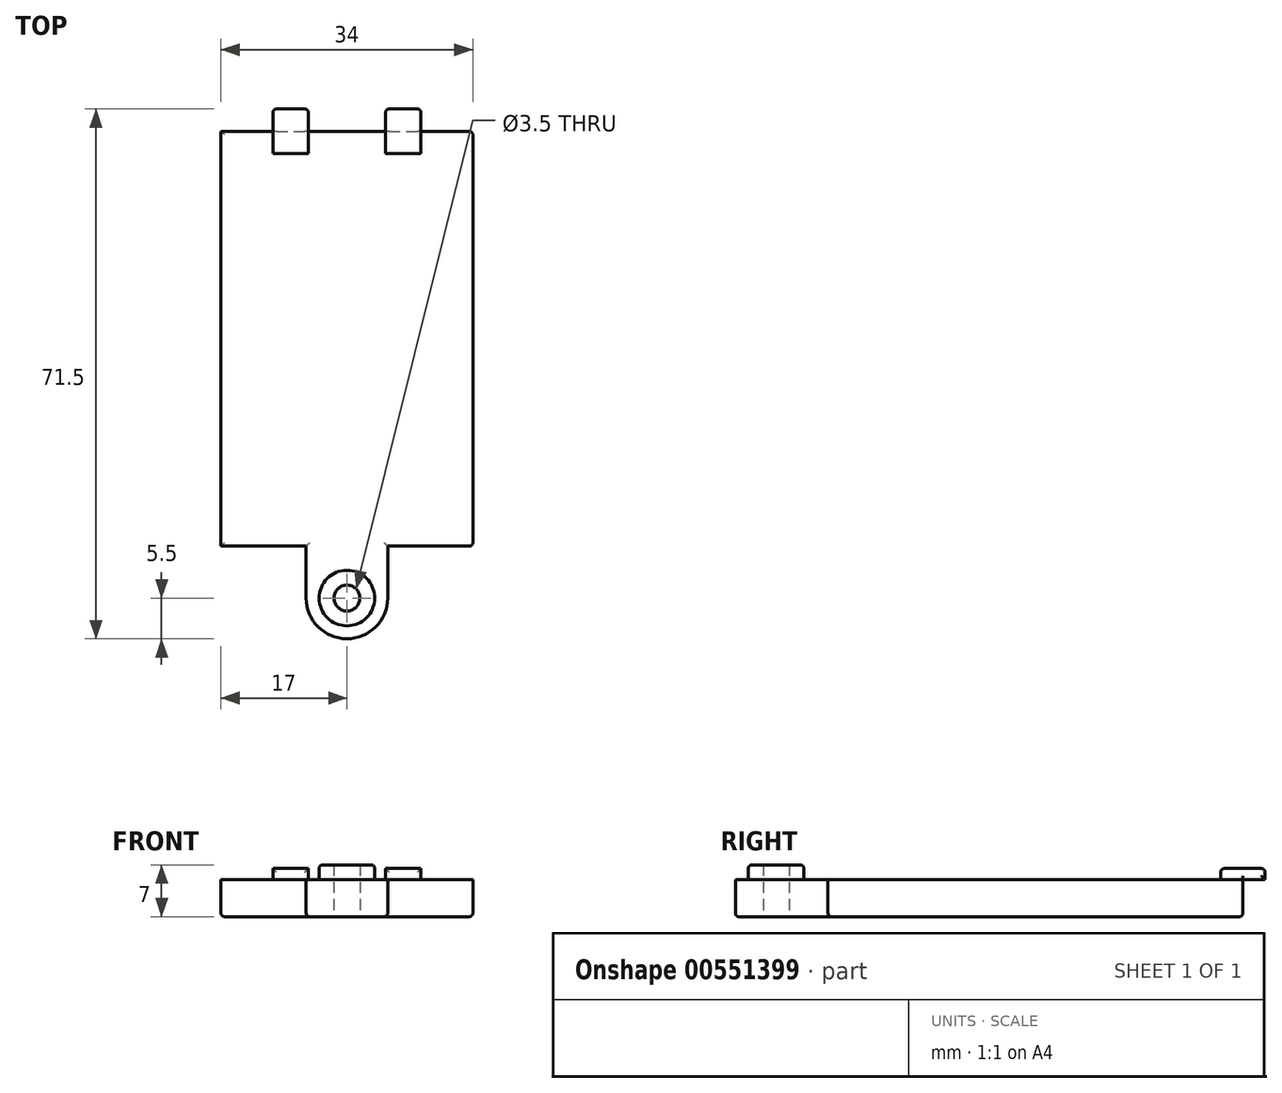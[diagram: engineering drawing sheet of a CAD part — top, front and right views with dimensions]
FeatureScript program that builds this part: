
annotation { "Feature Type Name" : "Feature", "Feature Type Description" : "" }
export const myFeature = defineFeature(function(context is Context, id is Id, definition is map)
    precondition{}
    {
        {
            var Q0;
            Q0=qCreatedBy(makeId("Top.planeOp"),FACE);
            var sketch = newSketch(context, id + "F0", { "sketchPlane" : qUnion([Q0])});
            skLineSegment(sketch, "E0.bottom", {"start": v(-17, 29) * mm, "end": v(17, 29) * mm});
            skLineSegment(sketch, "E0.top", {"start": v(-17, -27) * mm, "end": v(17, -27) * mm});
            skLineSegment(sketch, "E0.left", {"start": v(-17, 29) * mm, "end": v(-17, -27) * mm});
            skLineSegment(sketch, "E0.right", {"start": v(17, 29) * mm, "end": v(17, -27) * mm});
            skCircle(sketch, "E1", {"center": v(0, -34) * mm, "radius": 5.5 * mm});
            skLineSegment(sketch, "E2", {"start": v(5.5, -34) * mm, "end": v(5.5, -27) * mm});
            skLineSegment(sketch, "E3", {"start": v(-5.5, -34) * mm, "end": v(-5.5, -27) * mm});
            skSolve(sketch);
        }
        {
            var Q0;
            Q0 = qSketchRegion(id + "F0", true);
            extrude(context, id + "F1", {"entities" : qUnion([Q0]), "depth" : 5 * mm, "offsetDistance" : 25 * mm});
        }
        {
            var Q0;
            Q0=makeQuery(id+"F1.opExtrude","CAP_FACE",FACE,{"disambiguationData":[OSD([sQuery(id+"F0.wireOp",EDGE,"E0.bottom"),sQuery(id+"F0.wireOp",EDGE,"E0.top"),sQuery(id+"F0.wireOp",EDGE,"E0.left"),sQuery(id+"F0.wireOp",EDGE,"E0.right"),sQuery(id+"F0.wireOp",EDGE,"E1"),sQuery(id+"F0.wireOp",EDGE,"E2"),sQuery(id+"F0.wireOp",EDGE,"E3")])],"isStart":false});
            var sketch = newSketch(context, id + "F2", { "sketchPlane" : qUnion([Q0])});
            skCircle(sketch, "E4", {"center": v(0, -34) * mm, "radius": 3.75 * mm});
            skSolve(sketch);
        }
        {
            var Q0;
            Q0 = qSketchRegion(id + "F2", true);
            extrude(context, id + "F3", {"entities" : qUnion([Q0]), "operationType" : NewBodyOperationType.ADD, "depth" : 2 * mm, "offsetDistance" : 25 * mm});
        }
        {
            var Q0;
            Q0=sQuery(id+"F0.wireOp",VERTEX,"E1.center");
            var Q1;
            Q1=makeQuery(id+"F1.opExtrude","SWEPT_BODY",BODY,{"disambiguationData":[OSD([sQuery(id+"F0.wireOp",EDGE,"E0.bottom"),sQuery(id+"F0.wireOp",EDGE,"E0.top"),sQuery(id+"F0.wireOp",EDGE,"E0.left"),sQuery(id+"F0.wireOp",EDGE,"E0.right"),sQuery(id+"F0.wireOp",EDGE,"E1"),sQuery(id+"F0.wireOp",EDGE,"E2"),sQuery(id+"F0.wireOp",EDGE,"E3")])]});
            hole(context, id + "F4", {"style" : HoleStyle.SIMPLE, "endStyle" : HoleEndStyle.THROUGH, "oppositeDirection" : true, "holeDiameter" : 3.5 * mm, "tappedDepth" : 12 * mm, "tapClearance" : 3, "locations" : qUnion([Q0]), "scope" : qUnion([Q1])});
        }
        {
            var Q0;
            Q0=makeQuery(id+"F1.opExtrude","CAP_FACE",FACE,{"disambiguationData":[OSD([sQuery(id+"F0.wireOp",EDGE,"E0.bottom"),sQuery(id+"F0.wireOp",EDGE,"E0.top"),sQuery(id+"F0.wireOp",EDGE,"E0.left"),sQuery(id+"F0.wireOp",EDGE,"E0.right"),sQuery(id+"F0.wireOp",EDGE,"E1"),sQuery(id+"F0.wireOp",EDGE,"E2"),sQuery(id+"F0.wireOp",EDGE,"E3")])],"isStart":false});
            var sketch = newSketch(context, id + "F5", { "sketchPlane" : qUnion([Q0])});
            skLineSegment(sketch, "E5.bottom", {"start": v(-10, 26) * mm, "end": v(-5.2, 26) * mm});
            skLineSegment(sketch, "E5.top", {"start": v(-10, 32) * mm, "end": v(-5.2, 32) * mm});
            skLineSegment(sketch, "E5.left", {"start": v(-10, 26) * mm, "end": v(-10, 32) * mm});
            skLineSegment(sketch, "E5.right", {"start": v(-5.2, 26) * mm, "end": v(-5.2, 32) * mm});
            skLineSegment(sketch, "E6.bottom", {"start": v(5.2, 26) * mm, "end": v(10, 26) * mm});
            skLineSegment(sketch, "E6.top", {"start": v(5.2, 32) * mm, "end": v(10, 32) * mm});
            skLineSegment(sketch, "E6.left", {"start": v(5.2, 26) * mm, "end": v(5.2, 32) * mm});
            skLineSegment(sketch, "E6.right", {"start": v(10, 26) * mm, "end": v(10, 32) * mm});
            skSolve(sketch);
        }
        {
            var Q0;
            Q0 = qSketchRegion(id + "F5", true);
            extrude(context, id + "F6", {"entities" : qUnion([Q0]), "operationType" : NewBodyOperationType.ADD, "depth" : 1.5 * mm, "offsetDistance" : 25 * mm});
        }
        {
            var Q0;
            Q0=makeQuery(id+"F6.opExtrude","CAP_EDGE",EDGE,{"disambiguationData":[OSD([sQuery(id+"F5.wireOp",EDGE,"E6.bottom")])],"isStart":false});
            var Q1;
            Q1=makeQuery(id+"F6.opExtrude","CAP_EDGE",EDGE,{"disambiguationData":[OSD([sQuery(id+"F5.wireOp",EDGE,"E5.bottom")])],"isStart":false});
            var Q2;
            Q2=makeQuery(id+"F6.opExtrude","CAP_EDGE",EDGE,{"disambiguationData":[OSD([sQuery(id+"F5.wireOp",EDGE,"E5.top")])],"isStart":false});
            var Q3;
            Q3=makeQuery(id+"F6.opExtrude","CAP_EDGE",EDGE,{"disambiguationData":[OSD([sQuery(id+"F5.wireOp",EDGE,"E6.top")])],"isStart":false});
            var Q4;
            Q4=makeQuery(id+"F1.opExtrude","CAP_EDGE",EDGE,{"disambiguationData":[OSD([sQuery(id+"F0.wireOp",EDGE,"E0.bottom")])],"isStart":true});
            var Q5;
            Q5=makeQuery(id+"F1.opExtrude","SWEPT_EDGE",EDGE,{"disambiguationData":[OSD([sQuery(id+"F0.wireOp",EDGE,"E0.bottom"),sQuery(id+"F0.wireOp",EDGE,"E0.right")])]});
            var Q6;
            Q6=makeQuery(id+"F1.opExtrude","CAP_EDGE",EDGE,{"disambiguationData":[OSD([sQuery(id+"F0.wireOp",EDGE,"E0.right")])],"isStart":true});
            var Q7;
            Q7=makeQuery(id+"F1.opExtrude","SWEPT_EDGE",EDGE,{"disambiguationData":[OSD([sQuery(id+"F0.wireOp",EDGE,"E0.top"),sQuery(id+"F0.wireOp",EDGE,"E0.right")])]});
            var Q8;
            Q8=makeQuery(id+"F1.opExtrude","CAP_EDGE",EDGE,{"disambiguationData":[OSD([sQuery(id+"F0.wireOp",EDGE,"E2")])],"isStart":true});
            var Q9;
            Q9=makeQuery(id+"F1.opExtrude","CAP_EDGE",EDGE,{"disambiguationData":[OSD([sQuery(id+"F0.wireOp",EDGE,"E1")])],"isStart":true});
            var Q10;
            Q10=makeQuery(id+"F3.opExtrude","CAP_EDGE",EDGE,{"disambiguationData":[OSD([sQuery(id+"F2.wireOp",EDGE,"E4")])],"isStart":false});
            var Q11;
            {var subQ0=sQuery(id+"F0.wireOp",EDGE,"E0.top");Q11=makeQuery(id+"F1.opExtrude","CAP_EDGE",EDGE,{"disambiguationData":[OSD([subQ0]),TDD([makeQuery(id+"F0.imprint","IMPRINT",EDGE,{"disambiguationData":[TD([[makeQuery(id+"F0.imprint","INTERSECT",VERTEX,{"derivedFrom":[subQ0,sQuery(id+"F0.wireOp",EDGE,"E0.right")]}),1.0]])],"derivedFrom":subQ0})])],"isStart":true});}
            var Q12;
            {var subQ0=sQuery(id+"F0.wireOp",EDGE,"E0.top");Q12=makeQuery(id+"F1.opExtrude","CAP_EDGE",EDGE,{"disambiguationData":[OSD([subQ0]),TDD([makeQuery(id+"F0.imprint","IMPRINT",EDGE,{"disambiguationData":[TD([[makeQuery(id+"F0.imprint","INTERSECT",VERTEX,{"derivedFrom":[subQ0,sQuery(id+"F0.wireOp",EDGE,"E0.left")]}),-1.0]])],"derivedFrom":subQ0})])],"isStart":true});}
            var Q13;
            Q13=makeQuery(id+"F1.opExtrude","CAP_EDGE",EDGE,{"disambiguationData":[OSD([sQuery(id+"F0.wireOp",EDGE,"E0.left")])],"isStart":true});
            var Q14;
            Q14=makeQuery(id+"F6.opExtrude","SWEPT_EDGE",EDGE,{"disambiguationData":[OSD([sQuery(id+"F5.wireOp",EDGE,"E6.top"),sQuery(id+"F5.wireOp",EDGE,"E6.right")])]});
            var Q15;
            Q15=makeQuery(id+"F6.opExtrude","SWEPT_EDGE",EDGE,{"disambiguationData":[OSD([sQuery(id+"F5.wireOp",EDGE,"E6.top"),sQuery(id+"F5.wireOp",EDGE,"E6.left")])]});
            var Q16;
            Q16=makeQuery(id+"F6.opExtrude","SWEPT_EDGE",EDGE,{"disambiguationData":[OSD([sQuery(id+"F5.wireOp",EDGE,"E5.top"),sQuery(id+"F5.wireOp",EDGE,"E5.right")])]});
            var Q17;
            Q17=makeQuery(id+"F6.opExtrude","SWEPT_EDGE",EDGE,{"disambiguationData":[OSD([sQuery(id+"F5.wireOp",EDGE,"E5.top"),sQuery(id+"F5.wireOp",EDGE,"E5.left")])]});
            var Q18;
            Q18=makeQuery(id+"F6.opExtrude","CAP_EDGE",EDGE,{"disambiguationData":[OSD([sQuery(id+"F5.wireOp",EDGE,"E5.bottom")])],"isStart":true});
            var Q19;
            Q19=makeQuery(id+"F6.opExtrude","CAP_EDGE",EDGE,{"disambiguationData":[OSD([sQuery(id+"F5.wireOp",EDGE,"E6.bottom")])],"isStart":true});
            var Q20;
            {var subQ0=sQuery(id+"F5.wireOp",EDGE,"E6.left");Q20=makeQuery(id+"F6.boolean.opBoolean","SPLIT",EDGE,{"disambiguationData":[topologyDisambiguationEdgeConnected([makeQuery(id+"F1.opExtrude","CAP_FACE",FACE,{"disambiguationData":[OSD([sQuery(id+"F0.wireOp",EDGE,"E0.bottom"),sQuery(id+"F0.wireOp",EDGE,"E0.top"),sQuery(id+"F0.wireOp",EDGE,"E0.left"),sQuery(id+"F0.wireOp",EDGE,"E0.right"),sQuery(id+"F0.wireOp",EDGE,"E1"),sQuery(id+"F0.wireOp",EDGE,"E2"),sQuery(id+"F0.wireOp",EDGE,"E3")])],"isStart":false})])],"derivedFrom":makeQuery(id+"F6.opExtrude","CAP_EDGE",EDGE,{"disambiguationData":[OSD([subQ0])],"isStart":true})});}
            var Q21;
            {var subQ0=sQuery(id+"F5.wireOp",EDGE,"E5.left");Q21=makeQuery(id+"F6.boolean.opBoolean","SPLIT",EDGE,{"disambiguationData":[topologyDisambiguationEdgeConnected([makeQuery(id+"F1.opExtrude","CAP_FACE",FACE,{"disambiguationData":[OSD([sQuery(id+"F0.wireOp",EDGE,"E0.bottom"),sQuery(id+"F0.wireOp",EDGE,"E0.top"),sQuery(id+"F0.wireOp",EDGE,"E0.left"),sQuery(id+"F0.wireOp",EDGE,"E0.right"),sQuery(id+"F0.wireOp",EDGE,"E1"),sQuery(id+"F0.wireOp",EDGE,"E2"),sQuery(id+"F0.wireOp",EDGE,"E3")])],"isStart":false})])],"derivedFrom":makeQuery(id+"F6.opExtrude","CAP_EDGE",EDGE,{"disambiguationData":[OSD([subQ0])],"isStart":true})});}
            var Q22;
            {var subQ0=sQuery(id+"F5.wireOp",EDGE,"E5.right");Q22=makeQuery(id+"F6.boolean.opBoolean","SPLIT",EDGE,{"disambiguationData":[topologyDisambiguationEdgeConnected([makeQuery(id+"F1.opExtrude","CAP_FACE",FACE,{"disambiguationData":[OSD([sQuery(id+"F0.wireOp",EDGE,"E0.bottom"),sQuery(id+"F0.wireOp",EDGE,"E0.top"),sQuery(id+"F0.wireOp",EDGE,"E0.left"),sQuery(id+"F0.wireOp",EDGE,"E0.right"),sQuery(id+"F0.wireOp",EDGE,"E1"),sQuery(id+"F0.wireOp",EDGE,"E2"),sQuery(id+"F0.wireOp",EDGE,"E3")])],"isStart":false})])],"derivedFrom":makeQuery(id+"F6.opExtrude","CAP_EDGE",EDGE,{"disambiguationData":[OSD([subQ0])],"isStart":true})});}
            var Q23;
            {var subQ0=sQuery(id+"F5.wireOp",EDGE,"E6.right");Q23=makeQuery(id+"F6.boolean.opBoolean","SPLIT",EDGE,{"disambiguationData":[topologyDisambiguationEdgeConnected([makeQuery(id+"F1.opExtrude","CAP_FACE",FACE,{"disambiguationData":[OSD([sQuery(id+"F0.wireOp",EDGE,"E0.bottom"),sQuery(id+"F0.wireOp",EDGE,"E0.top"),sQuery(id+"F0.wireOp",EDGE,"E0.left"),sQuery(id+"F0.wireOp",EDGE,"E0.right"),sQuery(id+"F0.wireOp",EDGE,"E1"),sQuery(id+"F0.wireOp",EDGE,"E2"),sQuery(id+"F0.wireOp",EDGE,"E3")])],"isStart":false})])],"derivedFrom":makeQuery(id+"F6.opExtrude","CAP_EDGE",EDGE,{"disambiguationData":[OSD([subQ0])],"isStart":true})});}
            fillet(context, id + "F7", {"entities" : qUnion([Q0, Q1, Q2, Q3, Q4, Q5, Q6, Q7, Q8, Q9, Q10, Q11, Q12, Q13, Q14, Q15, Q16, Q17, Q18, Q19, Q20, Q21, Q22, Q23]), "radius" : 0.5 * mm, "tangentPropagation" : true, "allowEdgeOverflow" : false});
        }
    });
